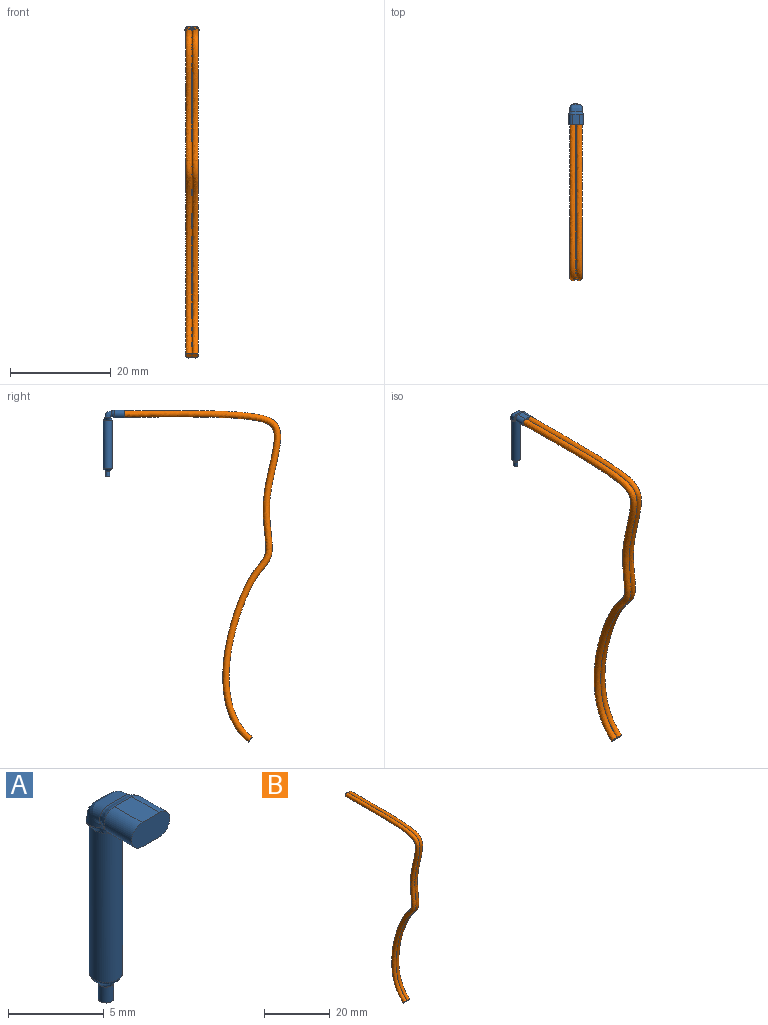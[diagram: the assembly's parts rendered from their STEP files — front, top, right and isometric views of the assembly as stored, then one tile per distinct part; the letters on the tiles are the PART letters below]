
ASSEMBLY  parts=2 mates=1
PART A: 12 faces, bbox 2.8x4.2x13.2 mm
  f0: plane 2.05x1.29mm, normal (0,0,1), area 2.6mm2, adj f1,f3,f4,f5
  f1: cylinder r=0.77mm len=2.03mm, axis (0,-1,0), area 4.9mm2, adj f0,f2,f4,f5
  f2: plane 2.05x1.29mm, normal (0,0,-1), area 2.6mm2, adj f1,f3,f4,f5
  f3: cylinder r=0.77mm len=2.03mm, axis (0,-1,0), area 4.9mm2, adj f0,f2,f4,f5
  f4: plane 2.82x1.55mm, normal (0,-1,0), area 3.9mm2, adj f0,f1,f2,f3
  f5: bspline ~2.82x1.55mm, area 3.7mm2, adj f0,f1,f2,f3,f6
  f6: bspline ~2.44x1.35mm, area 7.8mm2, adj f5,f7
  f7: bspline ~2.44x1.73mm, area 3.2mm2, adj f6,f8
  f8: cylinder r=0.86mm len=9.53mm, axis (0,0,1), area 51.7mm2, adj f7,f9
  f9: bspline ~1.73x1.73mm, area 3.2mm2, adj f8,f10
  f10: cylinder r=0.39mm len=1.02mm, axis (0,0,1), area 2.5mm2, adj f9,f11
  f11: plane 0.79x0.79mm, normal (0,0,-1), area 0.5mm2, adj f10
PART B: 6 faces, bbox 2.5x31.5x66.6 mm
  f0: plane 2.54x1.27mm, normal (0,1,0), area 2.5mm2, adj f2,f3,f4,f5
  f1: plane 2.54x0.99mm, normal (0,-0.78,-0.63), area 2.5mm2, adj f2,f3,f4,f5
  f2: bspline ~64.55x30.19mm, area 5.6mm2, adj f0,f1,f3,f5
  f3: bspline ~66.57x31.52mm, area 345.9mm2, adj f0,f1,f2,f4
  f4: bspline ~64.64x30.58mm, area 5.6mm2, adj f0,f1,f3,f5
  f5: bspline ~66.57x31.52mm, area 345.9mm2, adj f0,f1,f2,f4
PLACE A t=(1.59,-4.91,1.69)mm
PLACE B t=(1.59,-4.91,1.69)mm
MATE fastened A.f4 <-> B.f0  axis (0,-1,0) through (1.59,-4.91,1.69)mm
